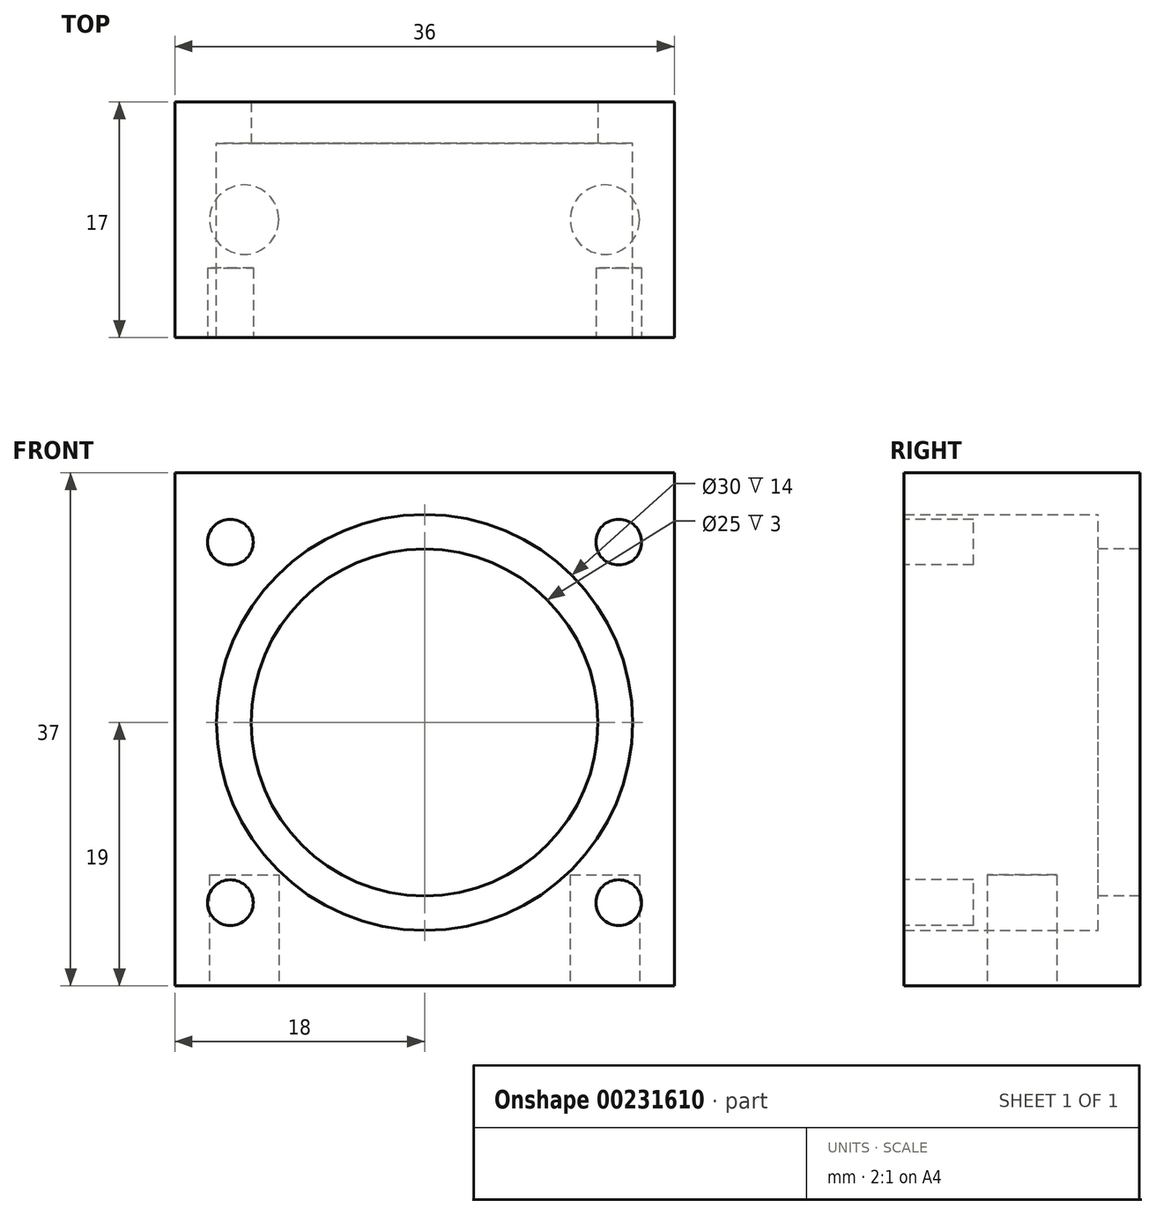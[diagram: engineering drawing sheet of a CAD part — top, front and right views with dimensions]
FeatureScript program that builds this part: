
annotation { "Feature Type Name" : "Feature", "Feature Type Description" : "" }
export const myFeature = defineFeature(function(context is Context, id is Id, definition is map)
    precondition{}
    {
        {
            var Q0;
            Q0=qCreatedBy(makeId("Front.planeOp"),FACE);
            var sketch = newSketch(context, id + "F0", { "sketchPlane" : qUnion([Q0])});
            skCircle(sketch, "E0", {"center": v(0, 0) * mm, "radius": 12.5 * mm});
            skCircle(sketch, "E1", {"center": v(0, 0) * mm, "radius": 15 * mm});
            skLineSegment(sketch, "E2.bottom", {"start": v(-18, 18) * mm, "end": v(18, 18) * mm});
            skLineSegment(sketch, "E2.top", {"start": v(-18, -19) * mm, "end": v(18, -19) * mm});
            skLineSegment(sketch, "E2.left", {"start": v(-18, 18) * mm, "end": v(-18, -19) * mm});
            skLineSegment(sketch, "E2.right", {"start": v(18, 18) * mm, "end": v(18, -19) * mm});
            skSolve(sketch);
        }
        {
            var Q0;
            Q0=makeQuery(id+"F0.imprint","IMPRINT",FACE,{"disambiguationData":[TD([[makeQuery(id+"F0.imprint","IMPRINT",EDGE,{"derivedFrom":sQuery(id+"F0.wireOp",EDGE,"E1")}),-1.0]])]});
            extrude(context, id + "F1", {"entities" : qUnion([Q0]), "depth" : 14 * mm});
        }
        {
            var Q0;
            Q0=makeQuery(id+"F0.imprint","IMPRINT",FACE,{"disambiguationData":[TD([[makeQuery(id+"F0.imprint","IMPRINT",EDGE,{"derivedFrom":sQuery(id+"F0.wireOp",EDGE,"E0")}),-1.0]])]});
            var Q1;
            Q1=makeQuery(id+"F0.imprint","IMPRINT",FACE,{"disambiguationData":[TD([[makeQuery(id+"F0.imprint","IMPRINT",EDGE,{"derivedFrom":sQuery(id+"F0.wireOp",EDGE,"E1")}),-1.0]])]});
            extrude(context, id + "F2", {"entities" : qUnion([Q0, Q1]), "operationType" : NewBodyOperationType.ADD, "oppositeDirection" : true, "depth" : 3 * mm});
        }
        {
            var Q0;
            Q0=makeQuery(id+"F1.opExtrude","CAP_FACE",FACE,{"disambiguationData":[OSD([sQuery(id+"F0.wireOp",EDGE,"E1"),sQuery(id+"F0.wireOp",EDGE,"E2.bottom"),sQuery(id+"F0.wireOp",EDGE,"E2.top"),sQuery(id+"F0.wireOp",EDGE,"E2.left"),sQuery(id+"F0.wireOp",EDGE,"E2.right")])],"isStart":false});
            var sketch = newSketch(context, id + "F3", { "sketchPlane" : qUnion([Q0])});
            skCircle(sketch, "E3", {"center": v(-14, 13) * mm, "radius": 1.65 * mm});
            skLineSegment(sketch, "E4.bottom", {"start": v(-14, 13) * mm, "end": v(14, 13) * mm, "construction": true});
            skLineSegment(sketch, "E4.top", {"start": v(-14, -13) * mm, "end": v(14, -13) * mm, "construction": true});
            skLineSegment(sketch, "E4.left", {"start": v(-14, 13) * mm, "end": v(-14, -13) * mm, "construction": true});
            skLineSegment(sketch, "E4.right", {"start": v(14, 13) * mm, "end": v(14, -13) * mm, "construction": true});
            skCircle(sketch, "E5", {"center": v(-14, -13) * mm, "radius": 1.65 * mm});
            skCircle(sketch, "E6", {"center": v(14, -13) * mm, "radius": 1.65 * mm});
            skCircle(sketch, "E7", {"center": v(14, 13) * mm, "radius": 1.65 * mm});
            skSolve(sketch);
        }
        {
            var Q0;
            Q0 = qSketchRegion(id + "F3", true);
            extrude(context, id + "F4", {"entities" : qUnion([Q0]), "operationType" : NewBodyOperationType.REMOVE, "oppositeDirection" : true, "depth" : 5 * mm});
        }
        {
            var Q0;
            {var subQ0=sQuery(id+"F0.wireOp",EDGE,"E2.top");Q0=makeQuery(id+"F2.boolean.opBoolean","MERGE",FACE,{"derivedFrom":[makeQuery(id+"F1.opExtrude","SWEPT_FACE",FACE,{"disambiguationData":[OSD([subQ0])]}),makeQuery(id+"F2.opExtrude","SWEPT_FACE",FACE,{"disambiguationData":[OSD([subQ0])]})]});}
            var sketch = newSketch(context, id + "F5", { "sketchPlane" : qUnion([Q0])});
            skLineSegment(sketch, "E8", {"start": v(-18, 5.5) * mm, "end": v(18, 5.5) * mm, "construction": true});
            skCircle(sketch, "E9", {"center": v(-13, 5.5) * mm, "radius": 2.5 * mm});
            skCircle(sketch, "E10", {"center": v(13, 5.5) * mm, "radius": 2.5 * mm});
            skSolve(sketch);
        }
        {
            var Q0;
            Q0 = qSketchRegion(id + "F5", true);
            extrude(context, id + "F6", {"entities" : qUnion([Q0]), "operationType" : NewBodyOperationType.REMOVE, "oppositeDirection" : true, "depth" : 8 * mm});
        }
    });
